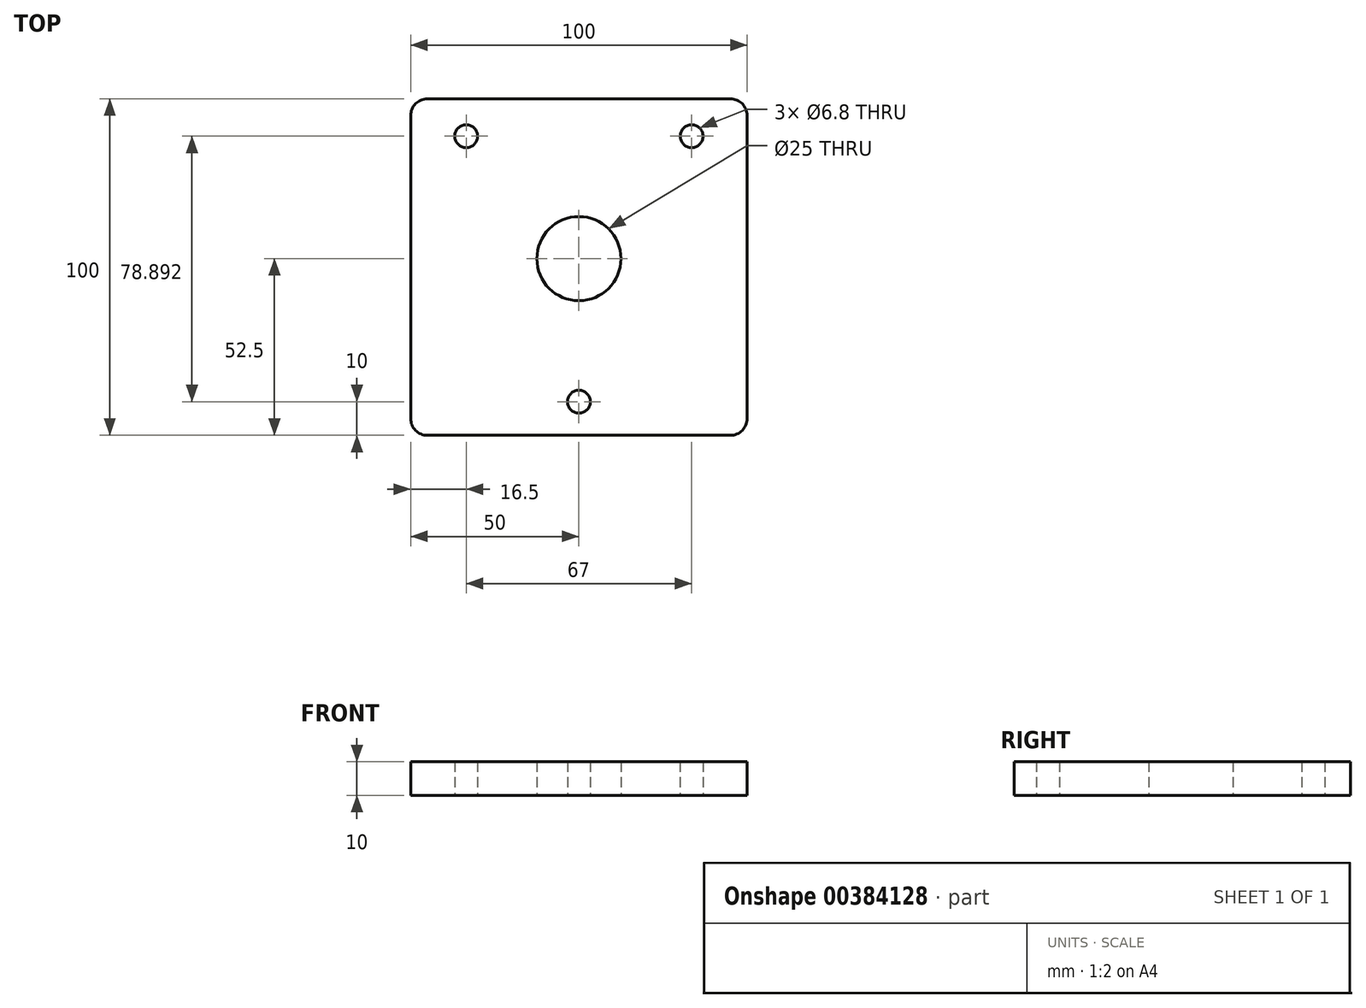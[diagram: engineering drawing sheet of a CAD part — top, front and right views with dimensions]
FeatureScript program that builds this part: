
annotation { "Feature Type Name" : "Feature", "Feature Type Description" : "" }
export const myFeature = defineFeature(function(context is Context, id is Id, definition is map)
    precondition{}
    {
        {
            var Q0;
            Q0=qCreatedBy(makeId("Top.planeOp"),FACE);
            var sketch = newSketch(context, id + "F0", { "sketchPlane" : qUnion([Q0])});
            skLineSegment(sketch, "E0.bottom", {"start": v(45, 50) * mm, "end": v(-45, 50) * mm});
            skLineSegment(sketch, "E0.top", {"start": v(45, -50) * mm, "end": v(-45, -50) * mm});
            skLineSegment(sketch, "E0.left", {"start": v(50, 45) * mm, "end": v(50, -45) * mm});
            skLineSegment(sketch, "E0.right", {"start": v(-50, 45) * mm, "end": v(-50, -45) * mm});
            skPoint(sketch, "E0.middle", {"position": v(0, 0) * mm});
            skPoint(sketch, "E1.visualSharp", {"position": v(-50, 50) * mm});
            skArc(sketch, "E1.filletArc", {"start": v(-45, 50) * mm, "mid": v(-48.54, 48.54) * mm, "end": v(-50, 45) * mm});
            skPoint(sketch, "E2.visualSharp", {"position": v(50, 50) * mm});
            skArc(sketch, "E2.filletArc", {"start": v(50, 45) * mm, "mid": v(48.54, 48.54) * mm, "end": v(45, 50) * mm});
            skPoint(sketch, "E3.visualSharp", {"position": v(50, -50) * mm});
            skArc(sketch, "E3.filletArc", {"start": v(45, -50) * mm, "mid": v(48.54, -48.54) * mm, "end": v(50, -45) * mm});
            skPoint(sketch, "E4.visualSharp", {"position": v(-50, -50) * mm});
            skArc(sketch, "E4.filletArc", {"start": v(-50, -45) * mm, "mid": v(-48.54, -48.54) * mm, "end": v(-45, -50) * mm});
            skCircle(sketch, "E5", {"center": v(-33.5, 38.9) * mm, "radius": 3.4 * mm});
            skCircle(sketch, "E6", {"center": v(33.5, 38.9) * mm, "radius": 3.4 * mm});
            skCircle(sketch, "E7", {"center": v(0, -40) * mm, "radius": 3.4 * mm});
            skCircle(sketch, "E8", {"center": v(0, 2.5) * mm, "radius": 12.5 * mm});
            skSolve(sketch);
        }
        {
            var Q0;
            Q0=makeQuery(id+"F0.imprint","IMPRINT",FACE,{"disambiguationData":[TD([[makeQuery(id+"F0.imprint","IMPRINT",EDGE,{"derivedFrom":sQuery(id+"F0.wireOp",EDGE,"E0.bottom")}),1.0]])]});
            extrude(context, id + "F1", {"entities" : qUnion([Q0]), "depth" : 10 * mm});
        }
    });
